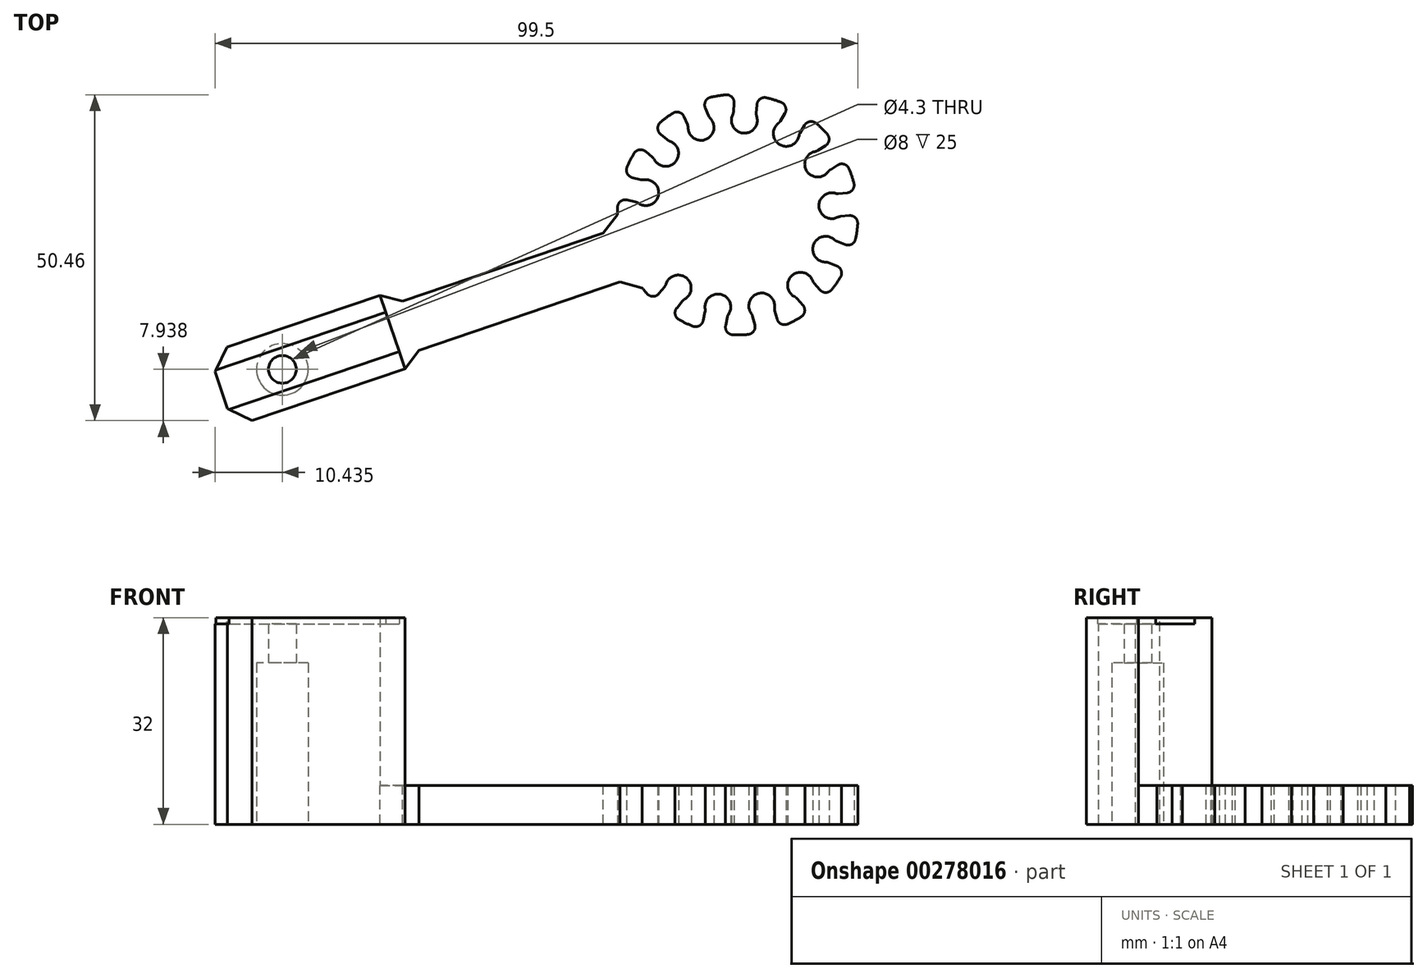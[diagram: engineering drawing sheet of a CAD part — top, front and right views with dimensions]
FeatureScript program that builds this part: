
annotation { "Feature Type Name" : "Feature", "Feature Type Description" : "" }
export const myFeature = defineFeature(function(context is Context, id is Id, definition is map)
    precondition{}
    {
        {
            var Q0;
            Q0=qCreatedBy(makeId("Top.planeOp"),FACE);
            var sketch = newSketch(context, id + "F0", { "sketchPlane" : qUnion([Q0])});
            skArc(sketch, "E0", {"start": v(-18.63, 0) * mm, "mid": v(-18.62, 0.59) * mm, "end": v(-18.6, 1.17) * mm});
            skArc(sketch, "E1", {"start": v(-9.98, 0) * mm, "mid": v(-9.7, 2.32) * mm, "end": v(-8.9, 4.51) * mm, "construction": true});
            skLineSegment(sketch, "E2", {"start": v(-18.63, 0) * mm, "end": v(0, 0) * mm, "construction": true});
            skLineSegment(sketch, "E3", {"start": v(0, 0) * mm, "end": v(-16.62, 8.42) * mm, "construction": true});
            skLineSegment(sketch, "E4", {"start": v(0, 0) * mm, "end": v(-12.29, 2.94) * mm, "construction": true});
            skArc(sketch, "E5", {"start": v(-15.38, 1.76) * mm, "mid": v(-12.29, 2.94) * mm, "end": v(-14.52, 5.38) * mm});
            skLineSegment(sketch, "E6", {"start": v(-14.97, 5.4) * mm, "end": v(-16.3, 5.72) * mm});
            skLineSegment(sketch, "E7", {"start": v(-15.8, 1.95) * mm, "end": v(-17.12, 2.26) * mm});
            skPoint(sketch, "E8", {"position": v(-9.7, 2.32) * mm});
            skLineSegment(sketch, "E9", {"start": v(-12.7, 6.43) * mm, "end": v(-13.33, 5.18) * mm, "construction": true});
            skLineSegment(sketch, "E10", {"start": v(-14.72, 5.34) * mm, "end": v(-15.54, 1.89) * mm, "construction": true});
            skArc(sketch, "E11.trimOffspring", {"start": v(-17.12, 7.36) * mm, "mid": v(-16.88, 7.9) * mm, "end": v(-16.62, 8.42) * mm});
            skPoint(sketch, "E12.visualSharp", {"position": v(-17.63, 6.04) * mm});
            skArc(sketch, "E12.filletArc", {"start": v(-17.12, 7.36) * mm, "mid": v(-17.09, 6.35) * mm, "end": v(-16.3, 5.72) * mm});
            skPoint(sketch, "E13.visualSharp", {"position": v(-18.45, 2.58) * mm});
            skArc(sketch, "E13.filletArc", {"start": v(-17.12, 2.26) * mm, "mid": v(-18.11, 2.06) * mm, "end": v(-18.6, 1.17) * mm});
            skPoint(sketch, "E14.visualSharp", {"position": v(-15.54, 1.89) * mm});
            skArc(sketch, "E14.filletArc", {"start": v(-15.38, 1.76) * mm, "mid": v(-15.58, 1.87) * mm, "end": v(-15.8, 1.95) * mm});
            skPoint(sketch, "E15.visualSharp", {"position": v(-14.72, 5.34) * mm});
            skArc(sketch, "E15.filletArc", {"start": v(-14.97, 5.4) * mm, "mid": v(-14.74, 5.37) * mm, "end": v(-14.52, 5.38) * mm});
            skArc(sketch, "E16.1.0", {"start": v(-16.62, 8.42) * mm, "mid": v(-16.35, 8.94) * mm, "end": v(-16.06, 9.45) * mm});
            skArc(sketch, "E16.1.1", {"start": v(-14.25, 9.76) * mm, "mid": v(-15.23, 10.03) * mm, "end": v(-16.06, 9.45) * mm});
            skLineSegment(sketch, "E16.1.2", {"start": v(-13.2, 8.87) * mm, "end": v(-14.25, 9.76) * mm});
            skArc(sketch, "E16.1.3", {"start": v(-12.92, 8.52) * mm, "mid": v(-13.05, 8.71) * mm, "end": v(-13.2, 8.87) * mm});
            skArc(sketch, "E16.1.4", {"start": v(-12.92, 8.52) * mm, "mid": v(-9.63, 8.17) * mm, "end": v(-10.52, 11.36) * mm});
            skArc(sketch, "E16.1.5", {"start": v(-10.91, 11.58) * mm, "mid": v(-10.73, 11.45) * mm, "end": v(-10.52, 11.36) * mm});
            skLineSegment(sketch, "E16.1.6", {"start": v(-10.91, 11.58) * mm, "end": v(-11.95, 12.47) * mm});
            skArc(sketch, "E16.1.7", {"start": v(-11.95, 14.3) * mm, "mid": v(-12.38, 13.38) * mm, "end": v(-11.95, 12.47) * mm});
            skArc(sketch, "E16.1.8", {"start": v(-11.95, 14.3) * mm, "mid": v(-11.49, 14.67) * mm, "end": v(-11.02, 15.03) * mm});
            skArc(sketch, "E16.2.0", {"start": v(-11.02, 15.03) * mm, "mid": v(-10.54, 15.36) * mm, "end": v(-10.05, 15.69) * mm});
            skArc(sketch, "E16.2.1", {"start": v(-8.3, 15.14) * mm, "mid": v(-9.05, 15.82) * mm, "end": v(-10.05, 15.69) * mm});
            skLineSegment(sketch, "E16.2.2", {"start": v(-7.77, 13.89) * mm, "end": v(-8.3, 15.14) * mm});
            skArc(sketch, "E16.2.3", {"start": v(-7.68, 13.45) * mm, "mid": v(-7.7, 13.67) * mm, "end": v(-7.77, 13.89) * mm});
            skArc(sketch, "E16.2.4", {"start": v(-7.68, 13.45) * mm, "mid": v(-4.9, 11.64) * mm, "end": v(-4.25, 14.89) * mm});
            skArc(sketch, "E16.2.5", {"start": v(-4.5, 15.26) * mm, "mid": v(-4.4, 15.06) * mm, "end": v(-4.25, 14.89) * mm});
            skLineSegment(sketch, "E16.2.6", {"start": v(-4.5, 15.26) * mm, "end": v(-5.03, 16.52) * mm});
            skArc(sketch, "E16.2.7", {"start": v(-4.2, 18.16) * mm, "mid": v(-5, 17.53) * mm, "end": v(-5.03, 16.52) * mm});
            skArc(sketch, "E16.2.8", {"start": v(-4.2, 18.16) * mm, "mid": v(-3.62, 18.28) * mm, "end": v(-3.04, 18.38) * mm});
            skLineSegment(sketch, "E16.anchor1", {"start": v(0, 0) * mm, "end": v(-18.63, 0) * mm, "construction": true});
            skLineSegment(sketch, "E16.anchor2", {"start": v(0, 0) * mm, "end": v(-8.04, -16.8) * mm, "construction": true});
            skArc(sketch, "E17.2.3.0", {"start": v(-3.04, 18.38) * mm, "mid": v(-2.46, 18.47) * mm, "end": v(-1.88, 18.54) * mm});
            skArc(sketch, "E17.4.3.0", {"start": v(-0.56, 17.26) * mm, "mid": v(-0.92, 18.2) * mm, "end": v(-1.88, 18.54) * mm});
            skLineSegment(sketch, "E17.8.3.0", {"start": v(-0.66, 15.9) * mm, "end": v(-0.56, 17.26) * mm});
            skArc(sketch, "E17.11.3.0", {"start": v(-0.77, 15.46) * mm, "mid": v(-0.7, 15.68) * mm, "end": v(-0.66, 15.9) * mm});
            skArc(sketch, "E17.15.3.0", {"start": v(-0.77, 15.46) * mm, "mid": v(0.9, 12.6) * mm, "end": v(2.94, 15.2) * mm});
            skArc(sketch, "E17.19.3.0", {"start": v(2.89, 15.65) * mm, "mid": v(2.9, 15.42) * mm, "end": v(2.94, 15.2) * mm});
            skLineSegment(sketch, "E17.23.3.0", {"start": v(2.89, 15.65) * mm, "end": v(2.98, 17.01) * mm});
            skArc(sketch, "E17.26.3.0", {"start": v(4.47, 18.1) * mm, "mid": v(3.47, 17.9) * mm, "end": v(2.98, 17.01) * mm});
            skArc(sketch, "E17.30.3.0", {"start": v(4.47, 18.1) * mm, "mid": v(5.03, 17.94) * mm, "end": v(5.6, 17.77) * mm});
            skArc(sketch, "E17.2.4.0", {"start": v(5.6, 17.77) * mm, "mid": v(6.15, 17.59) * mm, "end": v(6.7, 17.39) * mm});
            skArc(sketch, "E17.4.4.0", {"start": v(7.3, 15.65) * mm, "mid": v(7.4, 16.66) * mm, "end": v(6.7, 17.39) * mm});
            skLineSegment(sketch, "E17.8.4.0", {"start": v(6.6, 14.48) * mm, "end": v(7.3, 15.65) * mm});
            skArc(sketch, "E17.11.4.0", {"start": v(6.3, 14.14) * mm, "mid": v(6.47, 14.3) * mm, "end": v(6.6, 14.48) * mm});
            skArc(sketch, "E17.15.4.0", {"start": v(6.3, 14.14) * mm, "mid": v(6.5, 10.84) * mm, "end": v(9.5, 12.23) * mm});
            skArc(sketch, "E17.19.4.0", {"start": v(9.65, 12.65) * mm, "mid": v(9.55, 12.45) * mm, "end": v(9.5, 12.23) * mm});
            skLineSegment(sketch, "E17.23.4.0", {"start": v(9.65, 12.65) * mm, "end": v(10.35, 13.83) * mm});
            skArc(sketch, "E17.26.4.0", {"start": v(12.16, 14.12) * mm, "mid": v(11.19, 14.4) * mm, "end": v(10.35, 13.83) * mm});
            skArc(sketch, "E17.30.4.0", {"start": v(12.16, 14.12) * mm, "mid": v(12.6, 13.73) * mm, "end": v(13.03, 13.33) * mm});
            skArc(sketch, "E17.2.5.0", {"start": v(13.03, 13.33) * mm, "mid": v(13.44, 12.9) * mm, "end": v(13.84, 12.48) * mm});
            skArc(sketch, "E17.4.5.0", {"start": v(13.59, 10.66) * mm, "mid": v(14.14, 11.51) * mm, "end": v(13.84, 12.48) * mm});
            skLineSegment(sketch, "E17.8.5.0", {"start": v(12.43, 9.93) * mm, "end": v(13.59, 10.66) * mm});
            skArc(sketch, "E17.11.5.0", {"start": v(12.01, 9.77) * mm, "mid": v(12.23, 9.83) * mm, "end": v(12.43, 9.93) * mm});
            skArc(sketch, "E17.15.5.0", {"start": v(12.01, 9.77) * mm, "mid": v(10.69, 6.74) * mm, "end": v(14, 6.62) * mm});
            skArc(sketch, "E17.19.5.0", {"start": v(14.32, 6.93) * mm, "mid": v(14.15, 6.8) * mm, "end": v(14, 6.62) * mm});
            skLineSegment(sketch, "E17.23.5.0", {"start": v(14.32, 6.93) * mm, "end": v(15.48, 7.66) * mm});
            skArc(sketch, "E17.26.5.0", {"start": v(17.23, 7.1) * mm, "mid": v(16.48, 7.78) * mm, "end": v(15.48, 7.66) * mm});
            skArc(sketch, "E17.30.5.0", {"start": v(17.23, 7.1) * mm, "mid": v(17.44, 6.55) * mm, "end": v(17.64, 6) * mm});
            skArc(sketch, "E17.2.6.0", {"start": v(17.64, 6) * mm, "mid": v(17.82, 5.44) * mm, "end": v(17.98, 4.88) * mm});
            skArc(sketch, "E17.4.6.0", {"start": v(16.94, 3.37) * mm, "mid": v(17.81, 3.88) * mm, "end": v(17.98, 4.88) * mm});
            skLineSegment(sketch, "E17.8.6.0", {"start": v(15.58, 3.24) * mm, "end": v(16.94, 3.37) * mm});
            skArc(sketch, "E17.11.6.0", {"start": v(15.13, 3.28) * mm, "mid": v(15.35, 3.24) * mm, "end": v(15.58, 3.24) * mm});
            skArc(sketch, "E17.15.6.0", {"start": v(15.13, 3.28) * mm, "mid": v(12.58, 1.18) * mm, "end": v(15.48, -0.42) * mm});
            skArc(sketch, "E17.19.6.0", {"start": v(15.9, -0.3) * mm, "mid": v(15.69, -0.34) * mm, "end": v(15.48, -0.42) * mm});
            skLineSegment(sketch, "E17.23.6.0", {"start": v(15.9, -0.3) * mm, "end": v(17.27, -0.17) * mm});
            skArc(sketch, "E17.26.6.0", {"start": v(18.58, -1.45) * mm, "mid": v(18.22, -0.5) * mm, "end": v(17.27, -0.17) * mm});
            skArc(sketch, "E17.30.6.0", {"start": v(18.58, -1.45) * mm, "mid": v(18.52, -2.04) * mm, "end": v(18.45, -2.62) * mm});
            skArc(sketch, "E17.2.7.0", {"start": v(18.45, -2.62) * mm, "mid": v(18.36, -3.2) * mm, "end": v(18.25, -3.78) * mm});
            skArc(sketch, "E17.4.7.0", {"start": v(16.63, -4.65) * mm, "mid": v(17.64, -4.59) * mm, "end": v(18.25, -3.78) * mm});
            skLineSegment(sketch, "E17.8.7.0", {"start": v(15.36, -4.15) * mm, "end": v(16.63, -4.65) * mm});
            skArc(sketch, "E17.11.7.0", {"start": v(14.98, -3.9) * mm, "mid": v(15.16, -4.05) * mm, "end": v(15.36, -4.15) * mm});
            skArc(sketch, "E17.15.7.0", {"start": v(14.98, -3.9) * mm, "mid": v(11.75, -4.63) * mm, "end": v(13.62, -7.37) * mm});
            skArc(sketch, "E17.19.7.0", {"start": v(14.06, -7.45) * mm, "mid": v(13.84, -7.39) * mm, "end": v(13.62, -7.37) * mm});
            skLineSegment(sketch, "E17.23.7.0", {"start": v(14.06, -7.45) * mm, "end": v(15.33, -7.95) * mm});
            skArc(sketch, "E17.26.7.0", {"start": v(15.91, -9.7) * mm, "mid": v(16.03, -8.69) * mm, "end": v(15.33, -7.95) * mm});
            skArc(sketch, "E17.30.7.0", {"start": v(15.91, -9.7) * mm, "mid": v(15.6, -10.19) * mm, "end": v(15.27, -10.68) * mm});
            skArc(sketch, "E17.2.8.0", {"start": v(15.27, -10.68) * mm, "mid": v(14.93, -11.15) * mm, "end": v(14.57, -11.62) * mm});
            skArc(sketch, "E17.4.8.0", {"start": v(12.73, -11.67) * mm, "mid": v(13.66, -12.07) * mm, "end": v(14.57, -11.62) * mm});
            skLineSegment(sketch, "E17.8.8.0", {"start": v(11.83, -10.64) * mm, "end": v(12.73, -11.67) * mm});
            skArc(sketch, "E17.11.8.0", {"start": v(11.6, -10.26) * mm, "mid": v(11.7, -10.46) * mm, "end": v(11.83, -10.64) * mm});
            skArc(sketch, "E17.15.8.0", {"start": v(11.6, -10.26) * mm, "mid": v(8.39, -9.45) * mm, "end": v(8.82, -12.73) * mm});
            skArc(sketch, "E17.19.8.0", {"start": v(9.17, -13) * mm, "mid": v(9, -12.85) * mm, "end": v(8.82, -12.73) * mm});
            skLineSegment(sketch, "E17.23.8.0", {"start": v(9.17, -13) * mm, "end": v(10.08, -14.02) * mm});
            skArc(sketch, "E17.26.8.0", {"start": v(9.82, -15.84) * mm, "mid": v(10.37, -15) * mm, "end": v(10.08, -14.02) * mm});
            skArc(sketch, "E17.30.8.0", {"start": v(9.82, -15.84) * mm, "mid": v(9.31, -16.14) * mm, "end": v(8.8, -16.43) * mm});
            skArc(sketch, "E17.2.9.0", {"start": v(8.8, -16.43) * mm, "mid": v(8.28, -16.7) * mm, "end": v(7.75, -16.95) * mm});
            skArc(sketch, "E17.4.9.0", {"start": v(6.09, -16.16) * mm, "mid": v(6.73, -16.94) * mm, "end": v(7.75, -16.95) * mm});
            skLineSegment(sketch, "E17.8.9.0", {"start": v(5.74, -14.84) * mm, "end": v(6.09, -16.16) * mm});
            skArc(sketch, "E17.11.9.0", {"start": v(5.7, -14.4) * mm, "mid": v(5.7, -14.62) * mm, "end": v(5.74, -14.84) * mm});
            skArc(sketch, "E17.15.9.0", {"start": v(5.7, -14.4) * mm, "mid": v(3.21, -12.22) * mm, "end": v(2.11, -15.34) * mm});
            skArc(sketch, "E17.19.9.0", {"start": v(2.3, -15.74) * mm, "mid": v(2.23, -15.53) * mm, "end": v(2.11, -15.34) * mm});
            skLineSegment(sketch, "E17.23.9.0", {"start": v(2.3, -15.74) * mm, "end": v(2.65, -17.06) * mm});
            skArc(sketch, "E17.26.9.0", {"start": v(1.6, -18.57) * mm, "mid": v(2.47, -18.06) * mm, "end": v(2.65, -17.06) * mm});
            skArc(sketch, "E17.30.9.0", {"start": v(1.6, -18.57) * mm, "mid": v(1.01, -18.6) * mm, "end": v(0.42, -18.63) * mm});
            skArc(sketch, "E17.2.10.0", {"start": v(0.42, -18.63) * mm, "mid": v(-0.16, -18.63) * mm, "end": v(-0.75, -18.62) * mm});
            skArc(sketch, "E17.4.10.0", {"start": v(-1.87, -17.17) * mm, "mid": v(-1.65, -18.16) * mm, "end": v(-0.75, -18.62) * mm});
            skLineSegment(sketch, "E17.8.10.0", {"start": v(-1.59, -15.83) * mm, "end": v(-1.87, -17.17) * mm});
            skArc(sketch, "E17.11.10.0", {"start": v(-1.41, -15.42) * mm, "mid": v(-1.52, -15.62) * mm, "end": v(-1.59, -15.83) * mm});
            skArc(sketch, "E17.15.10.0", {"start": v(-1.41, -15.42) * mm, "mid": v(-2.65, -12.35) * mm, "end": v(-5.05, -14.64) * mm});
            skArc(sketch, "E17.19.10.0", {"start": v(-5.06, -15.09) * mm, "mid": v(-5.03, -14.86) * mm, "end": v(-5.05, -14.64) * mm});
            skLineSegment(sketch, "E17.23.10.0", {"start": v(-5.06, -15.09) * mm, "end": v(-5.34, -16.42) * mm});
            skArc(sketch, "E17.26.10.0", {"start": v(-6.97, -17.28) * mm, "mid": v(-5.96, -17.23) * mm, "end": v(-5.34, -16.42) * mm});
            skArc(sketch, "E17.30.10.0", {"start": v(-6.97, -17.28) * mm, "mid": v(-7.5, -17.05) * mm, "end": v(-8.04, -16.8) * mm});
            skArc(sketch, "E17.2.11.0", {"start": v(-8.04, -16.8) * mm, "mid": v(-8.57, -16.55) * mm, "end": v(-9.08, -16.27) * mm});
            skArc(sketch, "E17.4.11.0", {"start": v(-9.43, -14.47) * mm, "mid": v(-9.68, -15.45) * mm, "end": v(-9.08, -16.27) * mm});
            skLineSegment(sketch, "E17.8.11.0", {"start": v(-8.57, -13.4) * mm, "end": v(-9.43, -14.47) * mm});
            skArc(sketch, "E17.11.11.0", {"start": v(-8.23, -13.12) * mm, "mid": v(-8.41, -13.24) * mm, "end": v(-8.57, -13.4) * mm});
            skArc(sketch, "E17.15.11.0", {"start": v(-8.23, -13.12) * mm, "mid": v(-7.95, -9.82) * mm, "end": v(-11.12, -10.78) * mm});
            skArc(sketch, "E17.19.11.0", {"start": v(-11.33, -11.17) * mm, "mid": v(-11.2, -10.98) * mm, "end": v(-11.12, -10.78) * mm});
            skLineSegment(sketch, "E17.23.11.0", {"start": v(-11.33, -11.17) * mm, "end": v(-12.19, -12.23) * mm});
            skArc(sketch, "E17.26.11.0", {"start": v(-14.03, -12.27) * mm, "mid": v(-13.1, -12.68) * mm, "end": v(-12.19, -12.23) * mm});
            skArc(sketch, "E17.30.11.0", {"start": v(-14.03, -12.27) * mm, "mid": v(-14.4, -11.82) * mm, "end": v(-14.77, -11.36) * mm});
            skLineSegment(sketch, "E18", {"start": v(0, 0) * mm, "end": v(-79.95, -27.2) * mm, "construction": true});
            skLineSegment(sketch, "E19", {"start": v(-18.63, 0) * mm, "end": v(-14.77, -11.36) * mm, "construction": true});
            skPoint(sketch, "E20", {"position": v(-16.7, -5.68) * mm});
            skLineSegment(sketch, "E21", {"start": v(-18.63, 0) * mm, "end": v(-81.88, -21.51) * mm});
            skLineSegment(sketch, "E22", {"start": v(-14.77, -11.36) * mm, "end": v(-78.02, -32.87) * mm});
            skLineSegment(sketch, "E23", {"start": v(-81.88, -21.51) * mm, "end": v(-78.02, -32.87) * mm});
            skLineSegment(sketch, "E24", {"start": v(-44.01, -8.63) * mm, "end": v(-40.15, -20) * mm, "construction": true});
            skLineSegment(sketch, "E25", {"start": v(-55.38, -12.5) * mm, "end": v(-51.51, -23.86) * mm, "construction": true});
            skCircle(sketch, "E26", {"center": v(-70.48, -23.97) * mm, "radius": 2.15 * mm});
            skSolve(sketch);
        }
        {
            var Q0;
            Q0 = qSketchRegion(id + "F0", true);
            extrude(context, id + "F1", {"entities" : qUnion([Q0]), "depth" : 6 * mm});
        }
        {
            var Q0;
            Q0=makeQuery(id+"F1.opExtrude","CAP_FACE",FACE,{"disambiguationData":[OSD([sQuery(id+"F0.wireOp",EDGE,"E0"),sQuery(id+"F0.wireOp",EDGE,"E5"),sQuery(id+"F0.wireOp",EDGE,"E6"),sQuery(id+"F0.wireOp",EDGE,"E7"),sQuery(id+"F0.wireOp",EDGE,"E11.trimOffspring"),sQuery(id+"F0.wireOp",EDGE,"E12.filletArc"),sQuery(id+"F0.wireOp",EDGE,"E13.filletArc"),sQuery(id+"F0.wireOp",EDGE,"E14.filletArc"),sQuery(id+"F0.wireOp",EDGE,"E15.filletArc"),sQuery(id+"F0.wireOp",EDGE,"E16.1.0"),sQuery(id+"F0.wireOp",EDGE,"E16.1.1"),sQuery(id+"F0.wireOp",EDGE,"E16.1.2"),sQuery(id+"F0.wireOp",EDGE,"E16.1.3"),sQuery(id+"F0.wireOp",EDGE,"E16.1.4"),sQuery(id+"F0.wireOp",EDGE,"E16.1.5"),sQuery(id+"F0.wireOp",EDGE,"E16.1.6"),sQuery(id+"F0.wireOp",EDGE,"E16.1.7"),sQuery(id+"F0.wireOp",EDGE,"E16.1.8"),sQuery(id+"F0.wireOp",EDGE,"E16.2.0"),sQuery(id+"F0.wireOp",EDGE,"E16.2.1"),sQuery(id+"F0.wireOp",EDGE,"E16.2.2"),sQuery(id+"F0.wireOp",EDGE,"E16.2.3"),sQuery(id+"F0.wireOp",EDGE,"E16.2.4"),sQuery(id+"F0.wireOp",EDGE,"E16.2.5"),sQuery(id+"F0.wireOp",EDGE,"E16.2.6"),sQuery(id+"F0.wireOp",EDGE,"E16.2.7"),sQuery(id+"F0.wireOp",EDGE,"E16.2.8"),sQuery(id+"F0.wireOp",EDGE,"E17.2.3.0"),sQuery(id+"F0.wireOp",EDGE,"E17.4.3.0"),sQuery(id+"F0.wireOp",EDGE,"E17.8.3.0"),sQuery(id+"F0.wireOp",EDGE,"E17.11.3.0"),sQuery(id+"F0.wireOp",EDGE,"E17.15.3.0"),sQuery(id+"F0.wireOp",EDGE,"E17.19.3.0"),sQuery(id+"F0.wireOp",EDGE,"E17.23.3.0"),sQuery(id+"F0.wireOp",EDGE,"E17.26.3.0"),sQuery(id+"F0.wireOp",EDGE,"E17.30.3.0"),sQuery(id+"F0.wireOp",EDGE,"E17.2.4.0"),sQuery(id+"F0.wireOp",EDGE,"E17.4.4.0"),sQuery(id+"F0.wireOp",EDGE,"E17.8.4.0"),sQuery(id+"F0.wireOp",EDGE,"E17.11.4.0"),sQuery(id+"F0.wireOp",EDGE,"E17.15.4.0"),sQuery(id+"F0.wireOp",EDGE,"E17.19.4.0"),sQuery(id+"F0.wireOp",EDGE,"E17.23.4.0"),sQuery(id+"F0.wireOp",EDGE,"E17.26.4.0"),sQuery(id+"F0.wireOp",EDGE,"E17.30.4.0"),sQuery(id+"F0.wireOp",EDGE,"E17.2.5.0"),sQuery(id+"F0.wireOp",EDGE,"E17.4.5.0"),sQuery(id+"F0.wireOp",EDGE,"E17.8.5.0"),sQuery(id+"F0.wireOp",EDGE,"E17.11.5.0"),sQuery(id+"F0.wireOp",EDGE,"E17.15.5.0"),sQuery(id+"F0.wireOp",EDGE,"E17.19.5.0"),sQuery(id+"F0.wireOp",EDGE,"E17.23.5.0"),sQuery(id+"F0.wireOp",EDGE,"E17.26.5.0"),sQuery(id+"F0.wireOp",EDGE,"E17.30.5.0"),sQuery(id+"F0.wireOp",EDGE,"E17.2.6.0"),sQuery(id+"F0.wireOp",EDGE,"E17.4.6.0"),sQuery(id+"F0.wireOp",EDGE,"E17.8.6.0"),sQuery(id+"F0.wireOp",EDGE,"E17.11.6.0"),sQuery(id+"F0.wireOp",EDGE,"E17.15.6.0"),sQuery(id+"F0.wireOp",EDGE,"E17.19.6.0"),sQuery(id+"F0.wireOp",EDGE,"E17.23.6.0"),sQuery(id+"F0.wireOp",EDGE,"E17.26.6.0"),sQuery(id+"F0.wireOp",EDGE,"E17.30.6.0"),sQuery(id+"F0.wireOp",EDGE,"E17.2.7.0"),sQuery(id+"F0.wireOp",EDGE,"E17.4.7.0"),sQuery(id+"F0.wireOp",EDGE,"E17.8.7.0"),sQuery(id+"F0.wireOp",EDGE,"E17.11.7.0"),sQuery(id+"F0.wireOp",EDGE,"E17.15.7.0"),sQuery(id+"F0.wireOp",EDGE,"E17.19.7.0"),sQuery(id+"F0.wireOp",EDGE,"E17.23.7.0"),sQuery(id+"F0.wireOp",EDGE,"E17.26.7.0"),sQuery(id+"F0.wireOp",EDGE,"E17.30.7.0"),sQuery(id+"F0.wireOp",EDGE,"E17.2.8.0"),sQuery(id+"F0.wireOp",EDGE,"E17.4.8.0"),sQuery(id+"F0.wireOp",EDGE,"E17.8.8.0"),sQuery(id+"F0.wireOp",EDGE,"E17.11.8.0"),sQuery(id+"F0.wireOp",EDGE,"E17.15.8.0"),sQuery(id+"F0.wireOp",EDGE,"E17.19.8.0"),sQuery(id+"F0.wireOp",EDGE,"E17.23.8.0"),sQuery(id+"F0.wireOp",EDGE,"E17.26.8.0"),sQuery(id+"F0.wireOp",EDGE,"E17.30.8.0"),sQuery(id+"F0.wireOp",EDGE,"E17.2.9.0"),sQuery(id+"F0.wireOp",EDGE,"E17.4.9.0"),sQuery(id+"F0.wireOp",EDGE,"E17.8.9.0"),sQuery(id+"F0.wireOp",EDGE,"E17.11.9.0"),sQuery(id+"F0.wireOp",EDGE,"E17.15.9.0"),sQuery(id+"F0.wireOp",EDGE,"E17.19.9.0"),sQuery(id+"F0.wireOp",EDGE,"E17.23.9.0"),sQuery(id+"F0.wireOp",EDGE,"E17.26.9.0"),sQuery(id+"F0.wireOp",EDGE,"E17.30.9.0"),sQuery(id+"F0.wireOp",EDGE,"E17.2.10.0"),sQuery(id+"F0.wireOp",EDGE,"E17.4.10.0"),sQuery(id+"F0.wireOp",EDGE,"E17.8.10.0"),sQuery(id+"F0.wireOp",EDGE,"E17.11.10.0"),sQuery(id+"F0.wireOp",EDGE,"E17.15.10.0"),sQuery(id+"F0.wireOp",EDGE,"E17.19.10.0"),sQuery(id+"F0.wireOp",EDGE,"E17.23.10.0"),sQuery(id+"F0.wireOp",EDGE,"E17.26.10.0"),sQuery(id+"F0.wireOp",EDGE,"E17.30.10.0"),sQuery(id+"F0.wireOp",EDGE,"E17.2.11.0"),sQuery(id+"F0.wireOp",EDGE,"E17.4.11.0"),sQuery(id+"F0.wireOp",EDGE,"E17.8.11.0"),sQuery(id+"F0.wireOp",EDGE,"E17.11.11.0"),sQuery(id+"F0.wireOp",EDGE,"E17.15.11.0"),sQuery(id+"F0.wireOp",EDGE,"E17.19.11.0"),sQuery(id+"F0.wireOp",EDGE,"E17.23.11.0"),sQuery(id+"F0.wireOp",EDGE,"E17.26.11.0"),sQuery(id+"F0.wireOp",EDGE,"E17.30.11.0"),sQuery(id+"F0.wireOp",EDGE,"E21"),sQuery(id+"F0.wireOp",EDGE,"E22"),sQuery(id+"F0.wireOp",EDGE,"E23"),sQuery(id+"F0.wireOp",EDGE,"E26")])],"isStart":false});
            var Q1;
            Q1=makeQuery(id+"F1.opExtrude","CAP_FACE",FACE,{"disambiguationData":[OSD([sQuery(id+"F0.wireOp",EDGE,"E0"),sQuery(id+"F0.wireOp",EDGE,"E5"),sQuery(id+"F0.wireOp",EDGE,"E6"),sQuery(id+"F0.wireOp",EDGE,"E7"),sQuery(id+"F0.wireOp",EDGE,"E11.trimOffspring"),sQuery(id+"F0.wireOp",EDGE,"E12.filletArc"),sQuery(id+"F0.wireOp",EDGE,"E13.filletArc"),sQuery(id+"F0.wireOp",EDGE,"E14.filletArc"),sQuery(id+"F0.wireOp",EDGE,"E15.filletArc"),sQuery(id+"F0.wireOp",EDGE,"E16.1.0"),sQuery(id+"F0.wireOp",EDGE,"E16.1.1"),sQuery(id+"F0.wireOp",EDGE,"E16.1.2"),sQuery(id+"F0.wireOp",EDGE,"E16.1.3"),sQuery(id+"F0.wireOp",EDGE,"E16.1.4"),sQuery(id+"F0.wireOp",EDGE,"E16.1.5"),sQuery(id+"F0.wireOp",EDGE,"E16.1.6"),sQuery(id+"F0.wireOp",EDGE,"E16.1.7"),sQuery(id+"F0.wireOp",EDGE,"E16.1.8"),sQuery(id+"F0.wireOp",EDGE,"E16.2.0"),sQuery(id+"F0.wireOp",EDGE,"E16.2.1"),sQuery(id+"F0.wireOp",EDGE,"E16.2.2"),sQuery(id+"F0.wireOp",EDGE,"E16.2.3"),sQuery(id+"F0.wireOp",EDGE,"E16.2.4"),sQuery(id+"F0.wireOp",EDGE,"E16.2.5"),sQuery(id+"F0.wireOp",EDGE,"E16.2.6"),sQuery(id+"F0.wireOp",EDGE,"E16.2.7"),sQuery(id+"F0.wireOp",EDGE,"E16.2.8"),sQuery(id+"F0.wireOp",EDGE,"E17.2.3.0"),sQuery(id+"F0.wireOp",EDGE,"E17.4.3.0"),sQuery(id+"F0.wireOp",EDGE,"E17.8.3.0"),sQuery(id+"F0.wireOp",EDGE,"E17.11.3.0"),sQuery(id+"F0.wireOp",EDGE,"E17.15.3.0"),sQuery(id+"F0.wireOp",EDGE,"E17.19.3.0"),sQuery(id+"F0.wireOp",EDGE,"E17.23.3.0"),sQuery(id+"F0.wireOp",EDGE,"E17.26.3.0"),sQuery(id+"F0.wireOp",EDGE,"E17.30.3.0"),sQuery(id+"F0.wireOp",EDGE,"E17.2.4.0"),sQuery(id+"F0.wireOp",EDGE,"E17.4.4.0"),sQuery(id+"F0.wireOp",EDGE,"E17.8.4.0"),sQuery(id+"F0.wireOp",EDGE,"E17.11.4.0"),sQuery(id+"F0.wireOp",EDGE,"E17.15.4.0"),sQuery(id+"F0.wireOp",EDGE,"E17.19.4.0"),sQuery(id+"F0.wireOp",EDGE,"E17.23.4.0"),sQuery(id+"F0.wireOp",EDGE,"E17.26.4.0"),sQuery(id+"F0.wireOp",EDGE,"E17.30.4.0"),sQuery(id+"F0.wireOp",EDGE,"E17.2.5.0"),sQuery(id+"F0.wireOp",EDGE,"E17.4.5.0"),sQuery(id+"F0.wireOp",EDGE,"E17.8.5.0"),sQuery(id+"F0.wireOp",EDGE,"E17.11.5.0"),sQuery(id+"F0.wireOp",EDGE,"E17.15.5.0"),sQuery(id+"F0.wireOp",EDGE,"E17.19.5.0"),sQuery(id+"F0.wireOp",EDGE,"E17.23.5.0"),sQuery(id+"F0.wireOp",EDGE,"E17.26.5.0"),sQuery(id+"F0.wireOp",EDGE,"E17.30.5.0"),sQuery(id+"F0.wireOp",EDGE,"E17.2.6.0"),sQuery(id+"F0.wireOp",EDGE,"E17.4.6.0"),sQuery(id+"F0.wireOp",EDGE,"E17.8.6.0"),sQuery(id+"F0.wireOp",EDGE,"E17.11.6.0"),sQuery(id+"F0.wireOp",EDGE,"E17.15.6.0"),sQuery(id+"F0.wireOp",EDGE,"E17.19.6.0"),sQuery(id+"F0.wireOp",EDGE,"E17.23.6.0"),sQuery(id+"F0.wireOp",EDGE,"E17.26.6.0"),sQuery(id+"F0.wireOp",EDGE,"E17.30.6.0"),sQuery(id+"F0.wireOp",EDGE,"E17.2.7.0"),sQuery(id+"F0.wireOp",EDGE,"E17.4.7.0"),sQuery(id+"F0.wireOp",EDGE,"E17.8.7.0"),sQuery(id+"F0.wireOp",EDGE,"E17.11.7.0"),sQuery(id+"F0.wireOp",EDGE,"E17.15.7.0"),sQuery(id+"F0.wireOp",EDGE,"E17.19.7.0"),sQuery(id+"F0.wireOp",EDGE,"E17.23.7.0"),sQuery(id+"F0.wireOp",EDGE,"E17.26.7.0"),sQuery(id+"F0.wireOp",EDGE,"E17.30.7.0"),sQuery(id+"F0.wireOp",EDGE,"E17.2.8.0"),sQuery(id+"F0.wireOp",EDGE,"E17.4.8.0"),sQuery(id+"F0.wireOp",EDGE,"E17.8.8.0"),sQuery(id+"F0.wireOp",EDGE,"E17.11.8.0"),sQuery(id+"F0.wireOp",EDGE,"E17.15.8.0"),sQuery(id+"F0.wireOp",EDGE,"E17.19.8.0"),sQuery(id+"F0.wireOp",EDGE,"E17.23.8.0"),sQuery(id+"F0.wireOp",EDGE,"E17.26.8.0"),sQuery(id+"F0.wireOp",EDGE,"E17.30.8.0"),sQuery(id+"F0.wireOp",EDGE,"E17.2.9.0"),sQuery(id+"F0.wireOp",EDGE,"E17.4.9.0"),sQuery(id+"F0.wireOp",EDGE,"E17.8.9.0"),sQuery(id+"F0.wireOp",EDGE,"E17.11.9.0"),sQuery(id+"F0.wireOp",EDGE,"E17.15.9.0"),sQuery(id+"F0.wireOp",EDGE,"E17.19.9.0"),sQuery(id+"F0.wireOp",EDGE,"E17.23.9.0"),sQuery(id+"F0.wireOp",EDGE,"E17.26.9.0"),sQuery(id+"F0.wireOp",EDGE,"E17.30.9.0"),sQuery(id+"F0.wireOp",EDGE,"E17.2.10.0"),sQuery(id+"F0.wireOp",EDGE,"E17.4.10.0"),sQuery(id+"F0.wireOp",EDGE,"E17.8.10.0"),sQuery(id+"F0.wireOp",EDGE,"E17.11.10.0"),sQuery(id+"F0.wireOp",EDGE,"E17.15.10.0"),sQuery(id+"F0.wireOp",EDGE,"E17.19.10.0"),sQuery(id+"F0.wireOp",EDGE,"E17.23.10.0"),sQuery(id+"F0.wireOp",EDGE,"E17.26.10.0"),sQuery(id+"F0.wireOp",EDGE,"E17.30.10.0"),sQuery(id+"F0.wireOp",EDGE,"E17.2.11.0"),sQuery(id+"F0.wireOp",EDGE,"E17.4.11.0"),sQuery(id+"F0.wireOp",EDGE,"E17.8.11.0"),sQuery(id+"F0.wireOp",EDGE,"E17.11.11.0"),sQuery(id+"F0.wireOp",EDGE,"E17.15.11.0"),sQuery(id+"F0.wireOp",EDGE,"E17.19.11.0"),sQuery(id+"F0.wireOp",EDGE,"E17.23.11.0"),sQuery(id+"F0.wireOp",EDGE,"E17.26.11.0"),sQuery(id+"F0.wireOp",EDGE,"E17.30.11.0"),sQuery(id+"F0.wireOp",EDGE,"E21"),sQuery(id+"F0.wireOp",EDGE,"E22"),sQuery(id+"F0.wireOp",EDGE,"E23"),sQuery(id+"F0.wireOp",EDGE,"E26")])],"isStart":false});
            var Q2;
            Q2=makeQuery(id+"F1.opExtrude","CAP_FACE",FACE,{"disambiguationData":[OSD([sQuery(id+"F0.wireOp",EDGE,"E0"),sQuery(id+"F0.wireOp",EDGE,"E5"),sQuery(id+"F0.wireOp",EDGE,"E6"),sQuery(id+"F0.wireOp",EDGE,"E7"),sQuery(id+"F0.wireOp",EDGE,"E11.trimOffspring"),sQuery(id+"F0.wireOp",EDGE,"E12.filletArc"),sQuery(id+"F0.wireOp",EDGE,"E13.filletArc"),sQuery(id+"F0.wireOp",EDGE,"E14.filletArc"),sQuery(id+"F0.wireOp",EDGE,"E15.filletArc"),sQuery(id+"F0.wireOp",EDGE,"E16.1.0"),sQuery(id+"F0.wireOp",EDGE,"E16.1.1"),sQuery(id+"F0.wireOp",EDGE,"E16.1.2"),sQuery(id+"F0.wireOp",EDGE,"E16.1.3"),sQuery(id+"F0.wireOp",EDGE,"E16.1.4"),sQuery(id+"F0.wireOp",EDGE,"E16.1.5"),sQuery(id+"F0.wireOp",EDGE,"E16.1.6"),sQuery(id+"F0.wireOp",EDGE,"E16.1.7"),sQuery(id+"F0.wireOp",EDGE,"E16.1.8"),sQuery(id+"F0.wireOp",EDGE,"E16.2.0"),sQuery(id+"F0.wireOp",EDGE,"E16.2.1"),sQuery(id+"F0.wireOp",EDGE,"E16.2.2"),sQuery(id+"F0.wireOp",EDGE,"E16.2.3"),sQuery(id+"F0.wireOp",EDGE,"E16.2.4"),sQuery(id+"F0.wireOp",EDGE,"E16.2.5"),sQuery(id+"F0.wireOp",EDGE,"E16.2.6"),sQuery(id+"F0.wireOp",EDGE,"E16.2.7"),sQuery(id+"F0.wireOp",EDGE,"E16.2.8"),sQuery(id+"F0.wireOp",EDGE,"E17.2.3.0"),sQuery(id+"F0.wireOp",EDGE,"E17.4.3.0"),sQuery(id+"F0.wireOp",EDGE,"E17.8.3.0"),sQuery(id+"F0.wireOp",EDGE,"E17.11.3.0"),sQuery(id+"F0.wireOp",EDGE,"E17.15.3.0"),sQuery(id+"F0.wireOp",EDGE,"E17.19.3.0"),sQuery(id+"F0.wireOp",EDGE,"E17.23.3.0"),sQuery(id+"F0.wireOp",EDGE,"E17.26.3.0"),sQuery(id+"F0.wireOp",EDGE,"E17.30.3.0"),sQuery(id+"F0.wireOp",EDGE,"E17.2.4.0"),sQuery(id+"F0.wireOp",EDGE,"E17.4.4.0"),sQuery(id+"F0.wireOp",EDGE,"E17.8.4.0"),sQuery(id+"F0.wireOp",EDGE,"E17.11.4.0"),sQuery(id+"F0.wireOp",EDGE,"E17.15.4.0"),sQuery(id+"F0.wireOp",EDGE,"E17.19.4.0"),sQuery(id+"F0.wireOp",EDGE,"E17.23.4.0"),sQuery(id+"F0.wireOp",EDGE,"E17.26.4.0"),sQuery(id+"F0.wireOp",EDGE,"E17.30.4.0"),sQuery(id+"F0.wireOp",EDGE,"E17.2.5.0"),sQuery(id+"F0.wireOp",EDGE,"E17.4.5.0"),sQuery(id+"F0.wireOp",EDGE,"E17.8.5.0"),sQuery(id+"F0.wireOp",EDGE,"E17.11.5.0"),sQuery(id+"F0.wireOp",EDGE,"E17.15.5.0"),sQuery(id+"F0.wireOp",EDGE,"E17.19.5.0"),sQuery(id+"F0.wireOp",EDGE,"E17.23.5.0"),sQuery(id+"F0.wireOp",EDGE,"E17.26.5.0"),sQuery(id+"F0.wireOp",EDGE,"E17.30.5.0"),sQuery(id+"F0.wireOp",EDGE,"E17.2.6.0"),sQuery(id+"F0.wireOp",EDGE,"E17.4.6.0"),sQuery(id+"F0.wireOp",EDGE,"E17.8.6.0"),sQuery(id+"F0.wireOp",EDGE,"E17.11.6.0"),sQuery(id+"F0.wireOp",EDGE,"E17.15.6.0"),sQuery(id+"F0.wireOp",EDGE,"E17.19.6.0"),sQuery(id+"F0.wireOp",EDGE,"E17.23.6.0"),sQuery(id+"F0.wireOp",EDGE,"E17.26.6.0"),sQuery(id+"F0.wireOp",EDGE,"E17.30.6.0"),sQuery(id+"F0.wireOp",EDGE,"E17.2.7.0"),sQuery(id+"F0.wireOp",EDGE,"E17.4.7.0"),sQuery(id+"F0.wireOp",EDGE,"E17.8.7.0"),sQuery(id+"F0.wireOp",EDGE,"E17.11.7.0"),sQuery(id+"F0.wireOp",EDGE,"E17.15.7.0"),sQuery(id+"F0.wireOp",EDGE,"E17.19.7.0"),sQuery(id+"F0.wireOp",EDGE,"E17.23.7.0"),sQuery(id+"F0.wireOp",EDGE,"E17.26.7.0"),sQuery(id+"F0.wireOp",EDGE,"E17.30.7.0"),sQuery(id+"F0.wireOp",EDGE,"E17.2.8.0"),sQuery(id+"F0.wireOp",EDGE,"E17.4.8.0"),sQuery(id+"F0.wireOp",EDGE,"E17.8.8.0"),sQuery(id+"F0.wireOp",EDGE,"E17.11.8.0"),sQuery(id+"F0.wireOp",EDGE,"E17.15.8.0"),sQuery(id+"F0.wireOp",EDGE,"E17.19.8.0"),sQuery(id+"F0.wireOp",EDGE,"E17.23.8.0"),sQuery(id+"F0.wireOp",EDGE,"E17.26.8.0"),sQuery(id+"F0.wireOp",EDGE,"E17.30.8.0"),sQuery(id+"F0.wireOp",EDGE,"E17.2.9.0"),sQuery(id+"F0.wireOp",EDGE,"E17.4.9.0"),sQuery(id+"F0.wireOp",EDGE,"E17.8.9.0"),sQuery(id+"F0.wireOp",EDGE,"E17.11.9.0"),sQuery(id+"F0.wireOp",EDGE,"E17.15.9.0"),sQuery(id+"F0.wireOp",EDGE,"E17.19.9.0"),sQuery(id+"F0.wireOp",EDGE,"E17.23.9.0"),sQuery(id+"F0.wireOp",EDGE,"E17.26.9.0"),sQuery(id+"F0.wireOp",EDGE,"E17.30.9.0"),sQuery(id+"F0.wireOp",EDGE,"E17.2.10.0"),sQuery(id+"F0.wireOp",EDGE,"E17.4.10.0"),sQuery(id+"F0.wireOp",EDGE,"E17.8.10.0"),sQuery(id+"F0.wireOp",EDGE,"E17.11.10.0"),sQuery(id+"F0.wireOp",EDGE,"E17.15.10.0"),sQuery(id+"F0.wireOp",EDGE,"E17.19.10.0"),sQuery(id+"F0.wireOp",EDGE,"E17.23.10.0"),sQuery(id+"F0.wireOp",EDGE,"E17.26.10.0"),sQuery(id+"F0.wireOp",EDGE,"E17.30.10.0"),sQuery(id+"F0.wireOp",EDGE,"E17.2.11.0"),sQuery(id+"F0.wireOp",EDGE,"E17.4.11.0"),sQuery(id+"F0.wireOp",EDGE,"E17.8.11.0"),sQuery(id+"F0.wireOp",EDGE,"E17.11.11.0"),sQuery(id+"F0.wireOp",EDGE,"E17.15.11.0"),sQuery(id+"F0.wireOp",EDGE,"E17.19.11.0"),sQuery(id+"F0.wireOp",EDGE,"E17.23.11.0"),sQuery(id+"F0.wireOp",EDGE,"E17.26.11.0"),sQuery(id+"F0.wireOp",EDGE,"E17.30.11.0"),sQuery(id+"F0.wireOp",EDGE,"E21"),sQuery(id+"F0.wireOp",EDGE,"E22"),sQuery(id+"F0.wireOp",EDGE,"E23"),sQuery(id+"F0.wireOp",EDGE,"E26")])],"isStart":false});
            var sketch = newSketch(context, id + "F2", { "sketchPlane" : qUnion([Q0, Q1, Q2])});
            skLineSegment(sketch, "E27.0", {"start": v(-18.63, 0) * mm, "end": v(-55.38, -12.5) * mm, "construction": true});
            skLineSegment(sketch, "E28.0", {"start": v(-81.88, -21.51) * mm, "end": v(-78.02, -32.87) * mm});
            skLineSegment(sketch, "E29.0", {"start": v(-14.77, -11.36) * mm, "end": v(-51.51, -23.86) * mm, "construction": true});
            skLineSegment(sketch, "E30", {"start": v(-55.38, -12.5) * mm, "end": v(-51.51, -23.86) * mm});
            skLineSegment(sketch, "E31", {"start": v(-55.38, -12.5) * mm, "end": v(-81.88, -21.51) * mm});
            skLineSegment(sketch, "E32", {"start": v(-51.51, -23.86) * mm, "end": v(-78.02, -32.87) * mm});
            skCircle(sketch, "E33.0", {"center": v(-70.48, -23.97) * mm, "radius": 2.15 * mm});
            skSolve(sketch);
        }
        {
            var Q0;
            Q0 = qSketchRegion(id + "F2", true);
            extrude(context, id + "F3", {"entities" : qUnion([Q0]), "operationType" : NewBodyOperationType.ADD, "depth" : 25 * mm});
        }
        {
            var Q0;
            Q0=makeQuery(id+"F3.opExtrude","CAP_FACE",FACE,{"disambiguationData":[OSD([sQuery(id+"F2.wireOp",EDGE,"E28.0"),sQuery(id+"F2.wireOp",EDGE,"E30"),sQuery(id+"F2.wireOp",EDGE,"E31"),sQuery(id+"F2.wireOp",EDGE,"E32"),sQuery(id+"F2.wireOp",EDGE,"E33.0")])],"isStart":false});
            var sketch = newSketch(context, id + "F4", { "sketchPlane" : qUnion([Q0])});
            skLineSegment(sketch, "E34.0", {"start": v(-55.38, -12.5) * mm, "end": v(-81.88, -21.51) * mm});
            skLineSegment(sketch, "E35.0", {"start": v(-55.38, -12.5) * mm, "end": v(-54.47, -15.15) * mm});
            skLineSegment(sketch, "E36.0", {"start": v(-51.51, -23.86) * mm, "end": v(-78.02, -32.87) * mm});
            skLineSegment(sketch, "E37.0", {"start": v(-81.88, -21.51) * mm, "end": v(-80.98, -24.16) * mm});
            skLineSegment(sketch, "E38", {"start": v(-80.98, -24.16) * mm, "end": v(-54.47, -15.15) * mm});
            skLineSegment(sketch, "E39", {"start": v(-78.92, -30.22) * mm, "end": v(-52.41, -21.2) * mm});
            skLineSegment(sketch, "E40", {"start": v(-80.98, -24.16) * mm, "end": v(-78.92, -30.22) * mm, "construction": true});
            skLineSegment(sketch, "E41", {"start": v(-78.92, -30.22) * mm, "end": v(-78.02, -32.87) * mm});
            skLineSegment(sketch, "E42", {"start": v(-54.47, -15.15) * mm, "end": v(-52.41, -21.2) * mm, "construction": true});
            skLineSegment(sketch, "E43", {"start": v(-52.41, -21.2) * mm, "end": v(-51.51, -23.86) * mm});
            skSolve(sketch);
        }
        {
            var Q0;
            Q0 = qSketchRegion(id + "F4", true);
            extrude(context, id + "F5", {"entities" : qUnion([Q0]), "operationType" : NewBodyOperationType.ADD, "depth" : 1 * mm});
        }
        {
            var Q0;
            Q0=makeQuery(id+"F3.opExtrude","CAP_FACE",FACE,{"disambiguationData":[OSD([sQuery(id+"F2.wireOp",EDGE,"E28.0"),sQuery(id+"F2.wireOp",EDGE,"E30"),sQuery(id+"F2.wireOp",EDGE,"E31"),sQuery(id+"F2.wireOp",EDGE,"E32"),sQuery(id+"F2.wireOp",EDGE,"E33.0")])],"isStart":false});
            cPlane(context, id + "F6", {"entities" : qUnion([Q0]), "cplaneType" : CPlaneType.OFFSET, "offset" : 6 * mm, "oppositeDirection" : true, "width" : 150 * mm, "height" : 150 * mm});
        }
        {
            var Q0;
            Q0=makeQuery(id+"F1.opExtrude","CAP_FACE",FACE,{"disambiguationData":[OSD([sQuery(id+"F0.wireOp",EDGE,"E0"),sQuery(id+"F0.wireOp",EDGE,"E5"),sQuery(id+"F0.wireOp",EDGE,"E6"),sQuery(id+"F0.wireOp",EDGE,"E7"),sQuery(id+"F0.wireOp",EDGE,"E11.trimOffspring"),sQuery(id+"F0.wireOp",EDGE,"E12.filletArc"),sQuery(id+"F0.wireOp",EDGE,"E13.filletArc"),sQuery(id+"F0.wireOp",EDGE,"E14.filletArc"),sQuery(id+"F0.wireOp",EDGE,"E15.filletArc"),sQuery(id+"F0.wireOp",EDGE,"E16.1.0"),sQuery(id+"F0.wireOp",EDGE,"E16.1.1"),sQuery(id+"F0.wireOp",EDGE,"E16.1.2"),sQuery(id+"F0.wireOp",EDGE,"E16.1.3"),sQuery(id+"F0.wireOp",EDGE,"E16.1.4"),sQuery(id+"F0.wireOp",EDGE,"E16.1.5"),sQuery(id+"F0.wireOp",EDGE,"E16.1.6"),sQuery(id+"F0.wireOp",EDGE,"E16.1.7"),sQuery(id+"F0.wireOp",EDGE,"E16.1.8"),sQuery(id+"F0.wireOp",EDGE,"E16.2.0"),sQuery(id+"F0.wireOp",EDGE,"E16.2.1"),sQuery(id+"F0.wireOp",EDGE,"E16.2.2"),sQuery(id+"F0.wireOp",EDGE,"E16.2.3"),sQuery(id+"F0.wireOp",EDGE,"E16.2.4"),sQuery(id+"F0.wireOp",EDGE,"E16.2.5"),sQuery(id+"F0.wireOp",EDGE,"E16.2.6"),sQuery(id+"F0.wireOp",EDGE,"E16.2.7"),sQuery(id+"F0.wireOp",EDGE,"E16.2.8"),sQuery(id+"F0.wireOp",EDGE,"E17.2.3.0"),sQuery(id+"F0.wireOp",EDGE,"E17.4.3.0"),sQuery(id+"F0.wireOp",EDGE,"E17.8.3.0"),sQuery(id+"F0.wireOp",EDGE,"E17.11.3.0"),sQuery(id+"F0.wireOp",EDGE,"E17.15.3.0"),sQuery(id+"F0.wireOp",EDGE,"E17.19.3.0"),sQuery(id+"F0.wireOp",EDGE,"E17.23.3.0"),sQuery(id+"F0.wireOp",EDGE,"E17.26.3.0"),sQuery(id+"F0.wireOp",EDGE,"E17.30.3.0"),sQuery(id+"F0.wireOp",EDGE,"E17.2.4.0"),sQuery(id+"F0.wireOp",EDGE,"E17.4.4.0"),sQuery(id+"F0.wireOp",EDGE,"E17.8.4.0"),sQuery(id+"F0.wireOp",EDGE,"E17.11.4.0"),sQuery(id+"F0.wireOp",EDGE,"E17.15.4.0"),sQuery(id+"F0.wireOp",EDGE,"E17.19.4.0"),sQuery(id+"F0.wireOp",EDGE,"E17.23.4.0"),sQuery(id+"F0.wireOp",EDGE,"E17.26.4.0"),sQuery(id+"F0.wireOp",EDGE,"E17.30.4.0"),sQuery(id+"F0.wireOp",EDGE,"E17.2.5.0"),sQuery(id+"F0.wireOp",EDGE,"E17.4.5.0"),sQuery(id+"F0.wireOp",EDGE,"E17.8.5.0"),sQuery(id+"F0.wireOp",EDGE,"E17.11.5.0"),sQuery(id+"F0.wireOp",EDGE,"E17.15.5.0"),sQuery(id+"F0.wireOp",EDGE,"E17.19.5.0"),sQuery(id+"F0.wireOp",EDGE,"E17.23.5.0"),sQuery(id+"F0.wireOp",EDGE,"E17.26.5.0"),sQuery(id+"F0.wireOp",EDGE,"E17.30.5.0"),sQuery(id+"F0.wireOp",EDGE,"E17.2.6.0"),sQuery(id+"F0.wireOp",EDGE,"E17.4.6.0"),sQuery(id+"F0.wireOp",EDGE,"E17.8.6.0"),sQuery(id+"F0.wireOp",EDGE,"E17.11.6.0"),sQuery(id+"F0.wireOp",EDGE,"E17.15.6.0"),sQuery(id+"F0.wireOp",EDGE,"E17.19.6.0"),sQuery(id+"F0.wireOp",EDGE,"E17.23.6.0"),sQuery(id+"F0.wireOp",EDGE,"E17.26.6.0"),sQuery(id+"F0.wireOp",EDGE,"E17.30.6.0"),sQuery(id+"F0.wireOp",EDGE,"E17.2.7.0"),sQuery(id+"F0.wireOp",EDGE,"E17.4.7.0"),sQuery(id+"F0.wireOp",EDGE,"E17.8.7.0"),sQuery(id+"F0.wireOp",EDGE,"E17.11.7.0"),sQuery(id+"F0.wireOp",EDGE,"E17.15.7.0"),sQuery(id+"F0.wireOp",EDGE,"E17.19.7.0"),sQuery(id+"F0.wireOp",EDGE,"E17.23.7.0"),sQuery(id+"F0.wireOp",EDGE,"E17.26.7.0"),sQuery(id+"F0.wireOp",EDGE,"E17.30.7.0"),sQuery(id+"F0.wireOp",EDGE,"E17.2.8.0"),sQuery(id+"F0.wireOp",EDGE,"E17.4.8.0"),sQuery(id+"F0.wireOp",EDGE,"E17.8.8.0"),sQuery(id+"F0.wireOp",EDGE,"E17.11.8.0"),sQuery(id+"F0.wireOp",EDGE,"E17.15.8.0"),sQuery(id+"F0.wireOp",EDGE,"E17.19.8.0"),sQuery(id+"F0.wireOp",EDGE,"E17.23.8.0"),sQuery(id+"F0.wireOp",EDGE,"E17.26.8.0"),sQuery(id+"F0.wireOp",EDGE,"E17.30.8.0"),sQuery(id+"F0.wireOp",EDGE,"E17.2.9.0"),sQuery(id+"F0.wireOp",EDGE,"E17.4.9.0"),sQuery(id+"F0.wireOp",EDGE,"E17.8.9.0"),sQuery(id+"F0.wireOp",EDGE,"E17.11.9.0"),sQuery(id+"F0.wireOp",EDGE,"E17.15.9.0"),sQuery(id+"F0.wireOp",EDGE,"E17.19.9.0"),sQuery(id+"F0.wireOp",EDGE,"E17.23.9.0"),sQuery(id+"F0.wireOp",EDGE,"E17.26.9.0"),sQuery(id+"F0.wireOp",EDGE,"E17.30.9.0"),sQuery(id+"F0.wireOp",EDGE,"E17.2.10.0"),sQuery(id+"F0.wireOp",EDGE,"E17.4.10.0"),sQuery(id+"F0.wireOp",EDGE,"E17.8.10.0"),sQuery(id+"F0.wireOp",EDGE,"E17.11.10.0"),sQuery(id+"F0.wireOp",EDGE,"E17.15.10.0"),sQuery(id+"F0.wireOp",EDGE,"E17.19.10.0"),sQuery(id+"F0.wireOp",EDGE,"E17.23.10.0"),sQuery(id+"F0.wireOp",EDGE,"E17.26.10.0"),sQuery(id+"F0.wireOp",EDGE,"E17.30.10.0"),sQuery(id+"F0.wireOp",EDGE,"E17.2.11.0"),sQuery(id+"F0.wireOp",EDGE,"E17.4.11.0"),sQuery(id+"F0.wireOp",EDGE,"E17.8.11.0"),sQuery(id+"F0.wireOp",EDGE,"E17.11.11.0"),sQuery(id+"F0.wireOp",EDGE,"E17.15.11.0"),sQuery(id+"F0.wireOp",EDGE,"E17.19.11.0"),sQuery(id+"F0.wireOp",EDGE,"E17.23.11.0"),sQuery(id+"F0.wireOp",EDGE,"E17.26.11.0"),sQuery(id+"F0.wireOp",EDGE,"E17.30.11.0"),sQuery(id+"F0.wireOp",EDGE,"E21"),sQuery(id+"F0.wireOp",EDGE,"E22"),sQuery(id+"F0.wireOp",EDGE,"E23"),sQuery(id+"F0.wireOp",EDGE,"E26")])],"isStart":true});
            var sketch = newSketch(context, id + "F7", { "sketchPlane" : qUnion([Q0])});
            skCircle(sketch, "E44", {"center": v(-70.48, 23.97) * mm, "radius": 4 * mm});
            skSolve(sketch);
        }
        {
            var Q0;
            Q0 = qSketchRegion(id + "F7", true);
            var Q1;
            Q1=qCreatedBy(id+"F6.planeOp",FACE);
            extrude(context, id + "F8", {"entities" : qUnion([Q0]), "operationType" : NewBodyOperationType.REMOVE, "endBound" : BoundingType.UP_TO_SURFACE, "oppositeDirection" : true, "endBoundEntityFace" : qUnion([Q1]), "depth" : 25 * mm});
        }
        {
            var Q0;
            Q0=makeQuery(id+"F1.opExtrude","CAP_FACE",FACE,{"disambiguationData":[OSD([sQuery(id+"F0.wireOp",EDGE,"E0"),sQuery(id+"F0.wireOp",EDGE,"E5"),sQuery(id+"F0.wireOp",EDGE,"E6"),sQuery(id+"F0.wireOp",EDGE,"E7"),sQuery(id+"F0.wireOp",EDGE,"E11.trimOffspring"),sQuery(id+"F0.wireOp",EDGE,"E12.filletArc"),sQuery(id+"F0.wireOp",EDGE,"E13.filletArc"),sQuery(id+"F0.wireOp",EDGE,"E14.filletArc"),sQuery(id+"F0.wireOp",EDGE,"E15.filletArc"),sQuery(id+"F0.wireOp",EDGE,"E16.1.0"),sQuery(id+"F0.wireOp",EDGE,"E16.1.1"),sQuery(id+"F0.wireOp",EDGE,"E16.1.2"),sQuery(id+"F0.wireOp",EDGE,"E16.1.3"),sQuery(id+"F0.wireOp",EDGE,"E16.1.4"),sQuery(id+"F0.wireOp",EDGE,"E16.1.5"),sQuery(id+"F0.wireOp",EDGE,"E16.1.6"),sQuery(id+"F0.wireOp",EDGE,"E16.1.7"),sQuery(id+"F0.wireOp",EDGE,"E16.1.8"),sQuery(id+"F0.wireOp",EDGE,"E16.2.0"),sQuery(id+"F0.wireOp",EDGE,"E16.2.1"),sQuery(id+"F0.wireOp",EDGE,"E16.2.2"),sQuery(id+"F0.wireOp",EDGE,"E16.2.3"),sQuery(id+"F0.wireOp",EDGE,"E16.2.4"),sQuery(id+"F0.wireOp",EDGE,"E16.2.5"),sQuery(id+"F0.wireOp",EDGE,"E16.2.6"),sQuery(id+"F0.wireOp",EDGE,"E16.2.7"),sQuery(id+"F0.wireOp",EDGE,"E16.2.8"),sQuery(id+"F0.wireOp",EDGE,"E17.2.3.0"),sQuery(id+"F0.wireOp",EDGE,"E17.4.3.0"),sQuery(id+"F0.wireOp",EDGE,"E17.8.3.0"),sQuery(id+"F0.wireOp",EDGE,"E17.11.3.0"),sQuery(id+"F0.wireOp",EDGE,"E17.15.3.0"),sQuery(id+"F0.wireOp",EDGE,"E17.19.3.0"),sQuery(id+"F0.wireOp",EDGE,"E17.23.3.0"),sQuery(id+"F0.wireOp",EDGE,"E17.26.3.0"),sQuery(id+"F0.wireOp",EDGE,"E17.30.3.0"),sQuery(id+"F0.wireOp",EDGE,"E17.2.4.0"),sQuery(id+"F0.wireOp",EDGE,"E17.4.4.0"),sQuery(id+"F0.wireOp",EDGE,"E17.8.4.0"),sQuery(id+"F0.wireOp",EDGE,"E17.11.4.0"),sQuery(id+"F0.wireOp",EDGE,"E17.15.4.0"),sQuery(id+"F0.wireOp",EDGE,"E17.19.4.0"),sQuery(id+"F0.wireOp",EDGE,"E17.23.4.0"),sQuery(id+"F0.wireOp",EDGE,"E17.26.4.0"),sQuery(id+"F0.wireOp",EDGE,"E17.30.4.0"),sQuery(id+"F0.wireOp",EDGE,"E17.2.5.0"),sQuery(id+"F0.wireOp",EDGE,"E17.4.5.0"),sQuery(id+"F0.wireOp",EDGE,"E17.8.5.0"),sQuery(id+"F0.wireOp",EDGE,"E17.11.5.0"),sQuery(id+"F0.wireOp",EDGE,"E17.15.5.0"),sQuery(id+"F0.wireOp",EDGE,"E17.19.5.0"),sQuery(id+"F0.wireOp",EDGE,"E17.23.5.0"),sQuery(id+"F0.wireOp",EDGE,"E17.26.5.0"),sQuery(id+"F0.wireOp",EDGE,"E17.30.5.0"),sQuery(id+"F0.wireOp",EDGE,"E17.2.6.0"),sQuery(id+"F0.wireOp",EDGE,"E17.4.6.0"),sQuery(id+"F0.wireOp",EDGE,"E17.8.6.0"),sQuery(id+"F0.wireOp",EDGE,"E17.11.6.0"),sQuery(id+"F0.wireOp",EDGE,"E17.15.6.0"),sQuery(id+"F0.wireOp",EDGE,"E17.19.6.0"),sQuery(id+"F0.wireOp",EDGE,"E17.23.6.0"),sQuery(id+"F0.wireOp",EDGE,"E17.26.6.0"),sQuery(id+"F0.wireOp",EDGE,"E17.30.6.0"),sQuery(id+"F0.wireOp",EDGE,"E17.2.7.0"),sQuery(id+"F0.wireOp",EDGE,"E17.4.7.0"),sQuery(id+"F0.wireOp",EDGE,"E17.8.7.0"),sQuery(id+"F0.wireOp",EDGE,"E17.11.7.0"),sQuery(id+"F0.wireOp",EDGE,"E17.15.7.0"),sQuery(id+"F0.wireOp",EDGE,"E17.19.7.0"),sQuery(id+"F0.wireOp",EDGE,"E17.23.7.0"),sQuery(id+"F0.wireOp",EDGE,"E17.26.7.0"),sQuery(id+"F0.wireOp",EDGE,"E17.30.7.0"),sQuery(id+"F0.wireOp",EDGE,"E17.2.8.0"),sQuery(id+"F0.wireOp",EDGE,"E17.4.8.0"),sQuery(id+"F0.wireOp",EDGE,"E17.8.8.0"),sQuery(id+"F0.wireOp",EDGE,"E17.11.8.0"),sQuery(id+"F0.wireOp",EDGE,"E17.15.8.0"),sQuery(id+"F0.wireOp",EDGE,"E17.19.8.0"),sQuery(id+"F0.wireOp",EDGE,"E17.23.8.0"),sQuery(id+"F0.wireOp",EDGE,"E17.26.8.0"),sQuery(id+"F0.wireOp",EDGE,"E17.30.8.0"),sQuery(id+"F0.wireOp",EDGE,"E17.2.9.0"),sQuery(id+"F0.wireOp",EDGE,"E17.4.9.0"),sQuery(id+"F0.wireOp",EDGE,"E17.8.9.0"),sQuery(id+"F0.wireOp",EDGE,"E17.11.9.0"),sQuery(id+"F0.wireOp",EDGE,"E17.15.9.0"),sQuery(id+"F0.wireOp",EDGE,"E17.19.9.0"),sQuery(id+"F0.wireOp",EDGE,"E17.23.9.0"),sQuery(id+"F0.wireOp",EDGE,"E17.26.9.0"),sQuery(id+"F0.wireOp",EDGE,"E17.30.9.0"),sQuery(id+"F0.wireOp",EDGE,"E17.2.10.0"),sQuery(id+"F0.wireOp",EDGE,"E17.4.10.0"),sQuery(id+"F0.wireOp",EDGE,"E17.8.10.0"),sQuery(id+"F0.wireOp",EDGE,"E17.11.10.0"),sQuery(id+"F0.wireOp",EDGE,"E17.15.10.0"),sQuery(id+"F0.wireOp",EDGE,"E17.19.10.0"),sQuery(id+"F0.wireOp",EDGE,"E17.23.10.0"),sQuery(id+"F0.wireOp",EDGE,"E17.26.10.0"),sQuery(id+"F0.wireOp",EDGE,"E17.30.10.0"),sQuery(id+"F0.wireOp",EDGE,"E17.2.11.0"),sQuery(id+"F0.wireOp",EDGE,"E17.4.11.0"),sQuery(id+"F0.wireOp",EDGE,"E17.8.11.0"),sQuery(id+"F0.wireOp",EDGE,"E17.11.11.0"),sQuery(id+"F0.wireOp",EDGE,"E17.15.11.0"),sQuery(id+"F0.wireOp",EDGE,"E17.19.11.0"),sQuery(id+"F0.wireOp",EDGE,"E17.23.11.0"),sQuery(id+"F0.wireOp",EDGE,"E17.26.11.0"),sQuery(id+"F0.wireOp",EDGE,"E17.30.11.0"),sQuery(id+"F0.wireOp",EDGE,"E21"),sQuery(id+"F0.wireOp",EDGE,"E22"),sQuery(id+"F0.wireOp",EDGE,"E23"),sQuery(id+"F0.wireOp",EDGE,"E26")])],"isStart":false});
            var sketch = newSketch(context, id + "F9", { "sketchPlane" : qUnion([Q0])});
            skLineSegment(sketch, "E45", {"start": v(-18.63, 0) * mm, "end": v(-20.83, -2.86) * mm});
            skLineSegment(sketch, "E46", {"start": v(-20.83, -2.86) * mm, "end": v(-51.9, -13.42) * mm});
            skLineSegment(sketch, "E47", {"start": v(-51.9, -13.42) * mm, "end": v(-55.38, -12.5) * mm});
            skLineSegment(sketch, "E48", {"start": v(-55.38, -12.5) * mm, "end": v(-18.63, 0) * mm});
            skLineSegment(sketch, "E49", {"start": v(-14.77, -11.36) * mm, "end": v(-51.51, -23.86) * mm});
            skLineSegment(sketch, "E50", {"start": v(-51.51, -23.86) * mm, "end": v(-49.32, -21) * mm});
            skLineSegment(sketch, "E51", {"start": v(-49.32, -21) * mm, "end": v(-18.25, -10.43) * mm});
            skLineSegment(sketch, "E52", {"start": v(-18.25, -10.43) * mm, "end": v(-14.77, -11.36) * mm});
            skLineSegment(sketch, "E53", {"start": v(-51.9, -13.42) * mm, "end": v(-49.32, -21) * mm, "construction": true});
            skLineSegment(sketch, "E54", {"start": v(-20.83, -2.86) * mm, "end": v(-18.25, -10.43) * mm, "construction": true});
            skLineSegment(sketch, "E55", {"start": v(-19.54, -6.65) * mm, "end": v(-50.6, -17.21) * mm, "construction": true});
            skSolve(sketch);
        }
        {
            var Q0;
            Q0 = qSketchRegion(id + "F9", true);
            extrude(context, id + "F10", {"entities" : qUnion([Q0]), "operationType" : NewBodyOperationType.REMOVE, "endBound" : BoundingType.UP_TO_NEXT, "oppositeDirection" : true, "depth" : 25 * mm});
        }
        {
            var Q0;
            Q0=makeQuery(id+"F5.boolean.opBoolean","MERGE",EDGE,{"derivedFrom":[makeQuery(id+"F3.boolean.opBoolean","MERGE",EDGE,{"derivedFrom":[makeQuery(id+"F1.opExtrude","SWEPT_EDGE",EDGE,{"disambiguationData":[OSD([sQuery(id+"F0.wireOp",EDGE,"E22"),sQuery(id+"F0.wireOp",EDGE,"E23")])]}),makeQuery(id+"F3.opExtrude","SWEPT_EDGE",EDGE,{"disambiguationData":[OSD([sQuery(id+"F2.wireOp",EDGE,"E28.0"),sQuery(id+"F2.wireOp",EDGE,"E32")])]})]}),makeQuery(id+"F5.opExtrude","SWEPT_EDGE",EDGE,{"disambiguationData":[OSD([sQuery(id+"F4.wireOp",EDGE,"E36.0"),sQuery(id+"F4.wireOp",EDGE,"E41")])]})]});
            var Q1;
            Q1=makeQuery(id+"F5.boolean.opBoolean","MERGE",EDGE,{"derivedFrom":[makeQuery(id+"F3.boolean.opBoolean","MERGE",EDGE,{"derivedFrom":[makeQuery(id+"F1.opExtrude","SWEPT_EDGE",EDGE,{"disambiguationData":[OSD([sQuery(id+"F0.wireOp",EDGE,"E21"),sQuery(id+"F0.wireOp",EDGE,"E23")])]}),makeQuery(id+"F3.opExtrude","SWEPT_EDGE",EDGE,{"disambiguationData":[OSD([sQuery(id+"F2.wireOp",EDGE,"E28.0"),sQuery(id+"F2.wireOp",EDGE,"E31")])]})]}),makeQuery(id+"F5.opExtrude","SWEPT_EDGE",EDGE,{"disambiguationData":[OSD([sQuery(id+"F4.wireOp",EDGE,"E34.0"),sQuery(id+"F4.wireOp",EDGE,"E37.0")])]})]});
            chamfer(context, id + "F11", {"entities" : qUnion([Q0, Q1]), "width" : 3 * mm, "tangentPropagation" : true});
        }
    });
